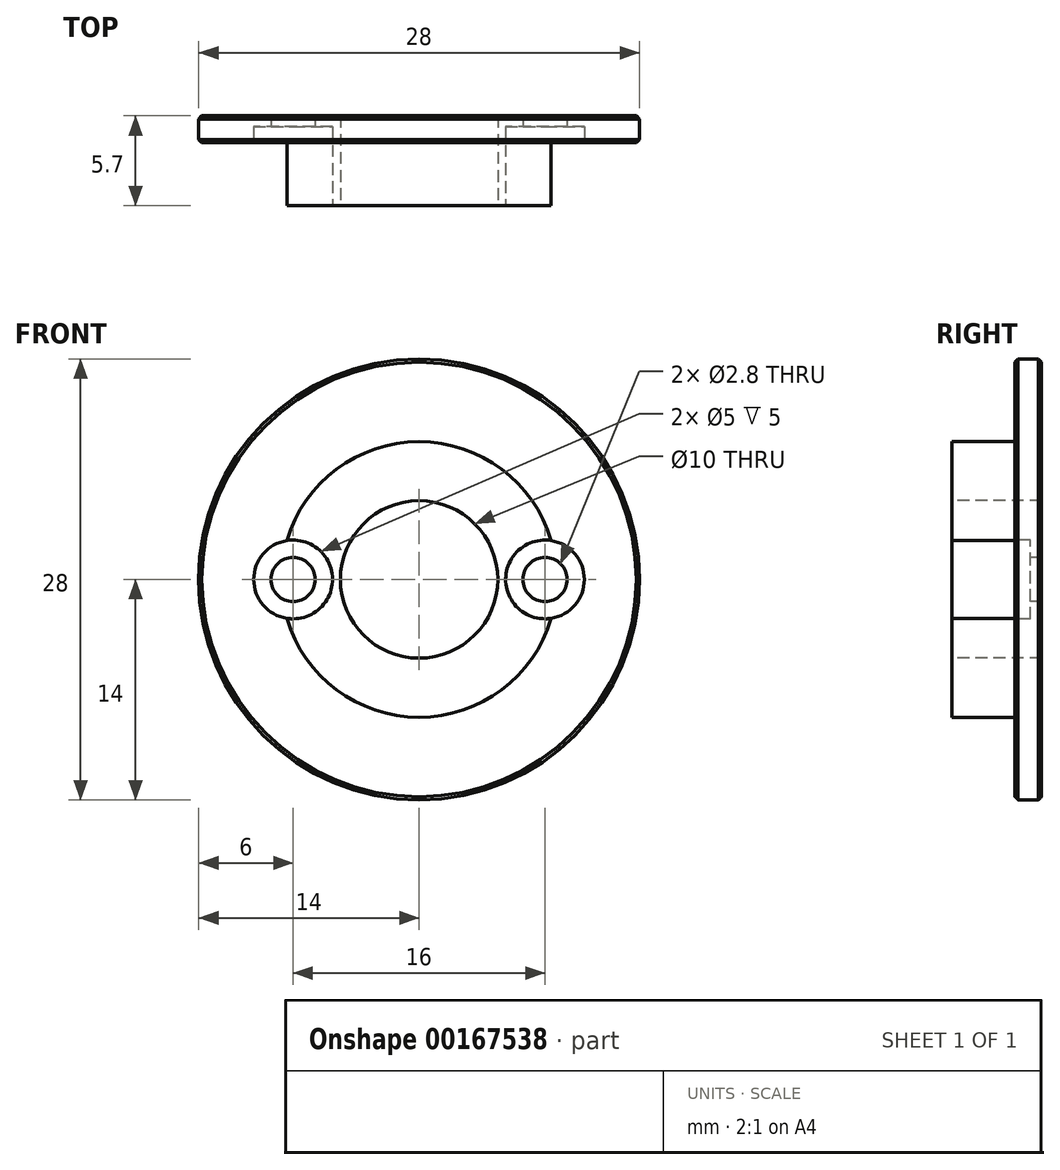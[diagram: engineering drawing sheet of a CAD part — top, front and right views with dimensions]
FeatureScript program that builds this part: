
annotation { "Feature Type Name" : "Feature", "Feature Type Description" : "" }
export const myFeature = defineFeature(function(context is Context, id is Id, definition is map)
    precondition{}
    {
        {
            var Q0;
            Q0=qCreatedBy(makeId("Front.planeOp"),FACE);
            var sketch = newSketch(context, id + "F0", { "sketchPlane" : qUnion([Q0])});
            skCircle(sketch, "E0", {"center": v(0, 0) * mm, "radius": 14 * mm});
            skCircle(sketch, "E1", {"center": v(0, 0) * mm, "radius": 8 * mm, "construction": true});
            skCircle(sketch, "E2", {"center": v(0, 0) * mm, "radius": 5 * mm});
            skLineSegment(sketch, "E3", {"start": v(-19.16, 0) * mm, "end": v(21.52, 0) * mm, "construction": true});
            skCircle(sketch, "E4", {"center": v(-8, 0) * mm, "radius": 1.4 * mm});
            skCircle(sketch, "E5.1.0", {"center": v(8, 0) * mm, "radius": 1.4 * mm});
            skSolve(sketch);
        }
        {
            var Q0;
            Q0=qSketchRegion(id+"F0",true);
            extrude(context, id + "F1", {"entities" : qUnion([Q0]), "oppositeDirection" : true, "depth" : 1.7 * mm});
        }
        {
            var Q0;
            Q0=makeQuery(id+"F1.opExtrude","CAP_EDGE",EDGE,{"disambiguationData":[OSD([sQuery(id+"F0.wireOp",EDGE,"E0")])],"isStart":false});
            var Q1;
            Q1=makeQuery(id+"F1.opExtrude","CAP_EDGE",EDGE,{"disambiguationData":[OSD([sQuery(id+"F0.wireOp",EDGE,"E0")])],"isStart":true});
            chamfer(context, id + "F2", {"entities" : qUnion([Q0, Q1]), "width" : 0.2 * mm, "tangentPropagation" : true});
        }
        {
            var Q0;
            Q0=makeQuery(id+"F1.opExtrude","CAP_FACE",FACE,{"disambiguationData":[OSD([sQuery(id+"F0.wireOp",EDGE,"E0"),sQuery(id+"F0.wireOp",EDGE,"E2"),sQuery(id+"F0.wireOp",EDGE,"E4"),sQuery(id+"F0.wireOp",EDGE,"E5.1.0")])],"isStart":true});
            var sketch = newSketch(context, id + "F3", { "sketchPlane" : qUnion([Q0])});
            skCircle(sketch, "E6.0", {"center": v(0, 0) * mm, "radius": 5 * mm});
            skArc(sketch, "E7", {"start": v(-8.66, -1.23) * mm, "mid": v(0, -8.75) * mm, "end": v(8.66, -1.23) * mm});
            skArc(sketch, "E8.0", {"start": v(-8.66, -1.23) * mm, "mid": v(-6.6, 0) * mm, "end": v(-8.66, 1.23) * mm});
            skArc(sketch, "E9.0", {"start": v(8.66, 1.23) * mm, "mid": v(6.6, 0) * mm, "end": v(8.66, -1.23) * mm});
            skArc(sketch, "E10.trimOffspring", {"start": v(8.66, 1.23) * mm, "mid": v(0, 8.75) * mm, "end": v(-8.66, 1.23) * mm});
            skSolve(sketch);
        }
        {
            var Q0;
            Q0=qSketchRegion(id+"F3",true);
            extrude(context, id + "F4", {"entities" : qUnion([Q0]), "operationType" : NewBodyOperationType.ADD, "depth" : 4 * mm});
        }
        {
            var Q0;
            Q0=makeQuery(id+"F1.opExtrude","CAP_FACE",FACE,{"disambiguationData":[OSD([sQuery(id+"F0.wireOp",EDGE,"E0"),sQuery(id+"F0.wireOp",EDGE,"E2"),sQuery(id+"F0.wireOp",EDGE,"E4"),sQuery(id+"F0.wireOp",EDGE,"E5.1.0")])],"isStart":true});
            var sketch = newSketch(context, id + "F5", { "sketchPlane" : qUnion([Q0])});
            skCircle(sketch, "E11.0", {"center": v(-8, 0) * mm, "radius": 1.4 * mm, "construction": true});
            skCircle(sketch, "E12.0", {"center": v(8, 0) * mm, "radius": 1.4 * mm, "construction": true});
            skCircle(sketch, "E13", {"center": v(-8, 0) * mm, "radius": 2.5 * mm});
            skCircle(sketch, "E14.1.0", {"center": v(8, 0) * mm, "radius": 2.5 * mm});
            skPoint(sketch, "E14.center", {"position": v(0, 0) * mm});
            skSolve(sketch);
        }
        {
            var Q0;
            Q0=qSketchRegion(id+"F5",true);
            extrude(context, id + "F6", {"entities" : qUnion([Q0]), "operationType" : NewBodyOperationType.REMOVE, "oppositeDirection" : true, "depth" : 1 * mm, "hasSecondDirection" : true, "secondDirectionBound" : BoundingType.THROUGH_ALL, "secondDirectionOppositeDirection" : false, "secondDirectionDepth" : 25 * mm});
        }
    });
